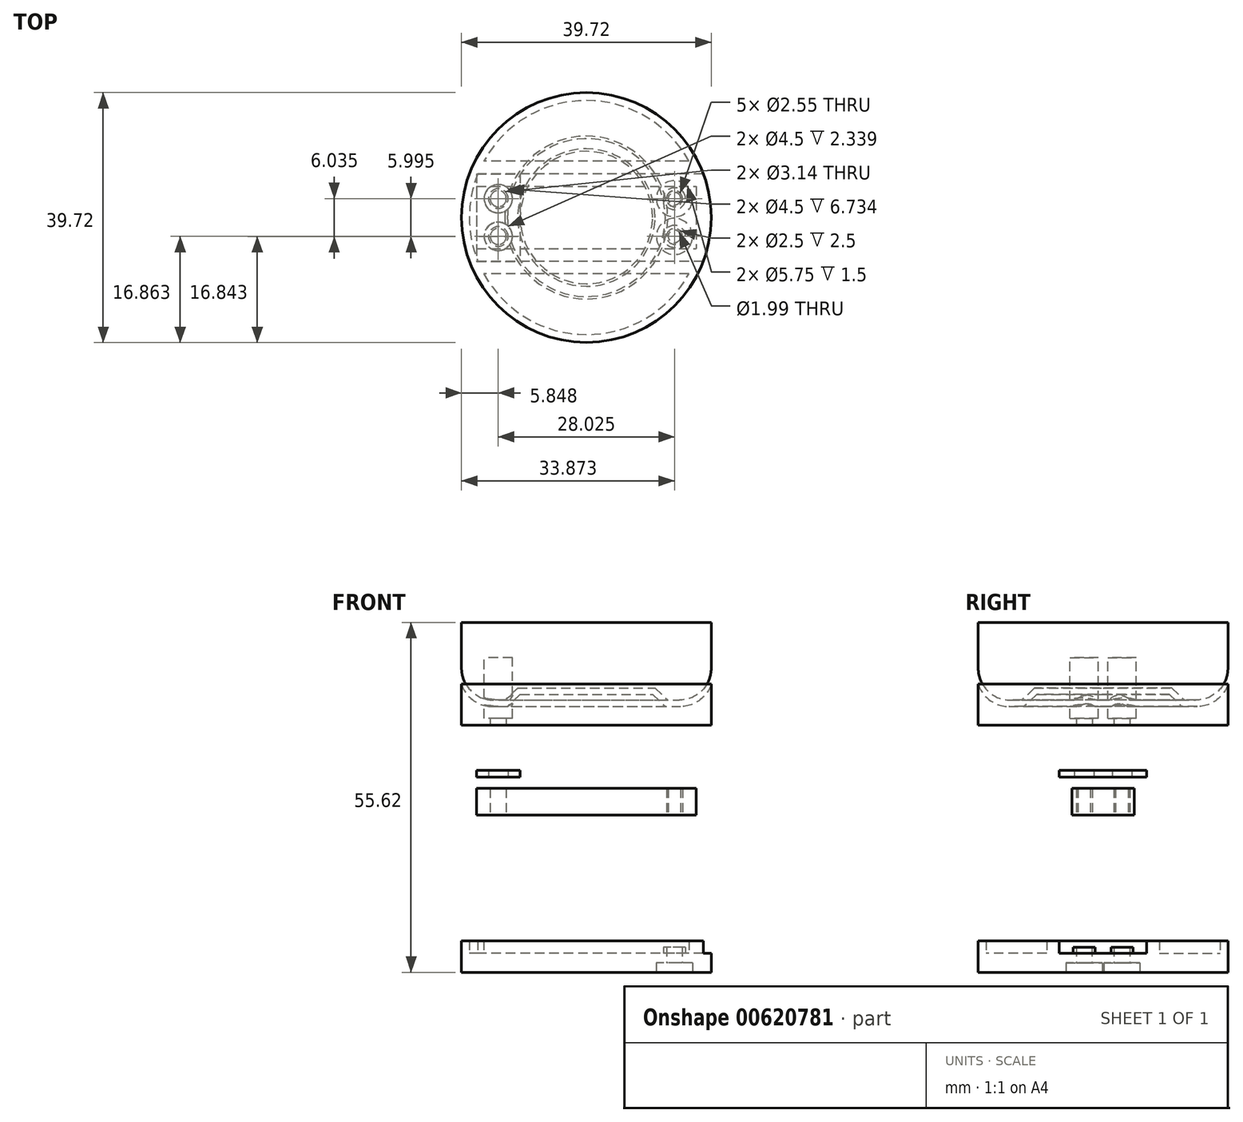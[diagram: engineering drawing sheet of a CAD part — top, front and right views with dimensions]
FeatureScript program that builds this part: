
annotation { "Feature Type Name" : "Feature", "Feature Type Description" : "" }
export const myFeature = defineFeature(function(context is Context, id is Id, definition is map)
    precondition{}
    {
        {
            var Q0;
            Q0=qCreatedBy(makeId("Front.planeOp"),FACE);
            var sketch = newSketch(context, id + "F0", { "sketchPlane" : qUnion([Q0])});
            skLineSegment(sketch, "E0", {"start": v(-12.95, 18.27) * mm, "end": v(-10.93, 20.17) * mm});
            skLineSegment(sketch, "E1", {"start": v(-12.95, 18.27) * mm, "end": v(-14.77, 18.27) * mm});
            skArc(sketch, "E2", {"start": v(-19.86, 23.36) * mm, "mid": v(-18.36, 19.76) * mm, "end": v(-14.77, 18.27) * mm});
            skLineSegment(sketch, "E3", {"start": v(-19.86, 23.36) * mm, "end": v(-19.86, 30.62) * mm});
            skLineSegment(sketch, "E4", {"start": v(0, 0) * mm, "end": v(0, 35.2) * mm, "construction": true});
            skLineSegment(sketch, "E5", {"start": v(-10.92, 20.17) * mm, "end": v(0, 20.17) * mm});
            skLineSegment(sketch, "E6", {"start": v(-19.86, 30.62) * mm, "end": v(0, 30.62) * mm});
            skLineSegment(sketch, "E7.MirrorCS", {"start": v(10.92, 20.17) * mm, "end": v(0, 20.17) * mm, "construction": true});
            skLineSegment(sketch, "E8.MirrorCS", {"start": v(19.86, 30.62) * mm, "end": v(0, 30.62) * mm, "construction": true});
            skLineSegment(sketch, "E9.MirrorCS", {"start": v(12.95, 18.27) * mm, "end": v(10.93, 20.17) * mm, "construction": true});
            skLineSegment(sketch, "E10.MirrorCS", {"start": v(19.86, 23.36) * mm, "end": v(19.86, 30.62) * mm, "construction": true});
            skLineSegment(sketch, "E11.MirrorCS", {"start": v(12.95, 18.27) * mm, "end": v(14.77, 18.27) * mm, "construction": true});
            skArc(sketch, "E12.MirrorCS", {"start": v(19.86, 23.36) * mm, "mid": v(18.36, 19.76) * mm, "end": v(14.77, 18.27) * mm, "construction": true});
            skLineSegment(sketch, "E13", {"start": v(0, 20.17) * mm, "end": v(0, 30.62) * mm});
            skLineSegment(sketch, "E14.0", {"start": v(-12.55, 17.27) * mm, "end": v(-15, 17.27) * mm});
            skLineSegment(sketch, "E14.1", {"start": v(-12.55, 17.27) * mm, "end": v(-10.53, 19.17) * mm});
            skLineSegment(sketch, "E14.2", {"start": v(-10.53, 19.17) * mm, "end": v(0, 19.17) * mm});
            skLineSegment(sketch, "E15", {"start": v(-19.86, 23.36) * mm, "end": v(-19.86, 8.22) * mm, "construction": true});
            skArc(sketch, "E16", {"start": v(-19.86, 20.85) * mm, "mid": v(-18.01, 18.26) * mm, "end": v(-15, 17.27) * mm});
            skLineSegment(sketch, "E17", {"start": v(0, 19.17) * mm, "end": v(0, 14.27) * mm});
            skLineSegment(sketch, "E18", {"start": v(0, 14.27) * mm, "end": v(-19.86, 14.27) * mm});
            skLineSegment(sketch, "E19", {"start": v(-19.86, 14.27) * mm, "end": v(-19.86, 20.85) * mm});
            skSolve(sketch);
        }
        {
            var Q0;
            Q0 = qSketchRegion(id + "F0", true);
            var Q1;
            Q1=sQuery(id+"F0.wireOp",EDGE,"E4");
            revolve(context, id + "F1", {"entities" : qUnion([Q0]), "axis" : qUnion([Q1]), "revolveType" : RevolveType.FULL});
        }
        {
            var Q0;
            Q0=qCreatedBy(makeId("Top.planeOp"),FACE);
            var sketch = newSketch(context, id + "F2", { "sketchPlane" : qUnion([Q0])});
            skLineSegment(sketch, "E20.bottom", {"start": v(-17.46, 4.95) * mm, "end": v(17.46, 4.95) * mm});
            skLineSegment(sketch, "E20.top", {"start": v(-17.46, -4.95) * mm, "end": v(17.46, -4.95) * mm});
            skLineSegment(sketch, "E20.left", {"start": v(-17.46, 4.95) * mm, "end": v(-17.46, -4.95) * mm});
            skLineSegment(sketch, "E20.right", {"start": v(17.46, 4.95) * mm, "end": v(17.46, -4.95) * mm});
            skPoint(sketch, "E20.middle", {"position": v(0, 0) * mm});
            skLineSegment(sketch, "E21", {"start": v(-57.83, 0) * mm, "end": v(44.3, 0) * mm, "construction": true});
            skLineSegment(sketch, "E22", {"start": v(0, -21.78) * mm, "end": v(0, 18.19) * mm, "construction": true});
            skCircle(sketch, "E23", {"center": v(-14.01, 3) * mm, "radius": 1 * mm});
            skCircle(sketch, "E24.MirrorC", {"center": v(-14.01, -3) * mm, "radius": 1 * mm});
            skCircle(sketch, "E25.MirrorC", {"center": v(14.01, 3) * mm, "radius": 1 * mm});
            skCircle(sketch, "E26.MirrorC", {"center": v(14.01, -3) * mm, "radius": 1 * mm});
            skCircle(sketch, "E27", {"center": v(-14.01, 3) * mm, "radius": 1.27 * mm});
            skCircle(sketch, "E28.MirrorC", {"center": v(14.01, 3) * mm, "radius": 1.27 * mm});
            skCircle(sketch, "E29.MirrorC", {"center": v(14.01, -3) * mm, "radius": 1.27 * mm});
            skCircle(sketch, "E30.MirrorC", {"center": v(-14.01, -3) * mm, "radius": 1.27 * mm});
            skCircle(sketch, "E31", {"center": v(0, 0) * mm, "radius": 19.86 * mm, "construction": true});
            skSolve(sketch);
        }
        {
            var Q0;
            Q0 = qSketchRegion(id + "F2", true);
            var Q1;
            Q1=makeQuery(id+"F2.imprint","IMPRINT",FACE,{"disambiguationData":[TD([[makeQuery(id+"F2.imprint","IMPRINT",EDGE,{"derivedFrom":sQuery(id+"F2.wireOp",EDGE,"E23")}),-1.0]])]});
            var Q2;
            Q2=makeQuery(id+"F2.imprint","IMPRINT",FACE,{"disambiguationData":[TD([[makeQuery(id+"F2.imprint","IMPRINT",EDGE,{"derivedFrom":sQuery(id+"F2.wireOp",EDGE,"E24.MirrorC")}),1.0]])]});
            var Q3;
            Q3=makeQuery(id+"F2.imprint","IMPRINT",FACE,{"disambiguationData":[TD([[makeQuery(id+"F2.imprint","IMPRINT",EDGE,{"derivedFrom":sQuery(id+"F2.wireOp",EDGE,"E25.MirrorC")}),1.0]])]});
            var Q4;
            Q4=makeQuery(id+"F2.imprint","IMPRINT",FACE,{"disambiguationData":[TD([[makeQuery(id+"F2.imprint","IMPRINT",EDGE,{"derivedFrom":sQuery(id+"F2.wireOp",EDGE,"E26.MirrorC")}),-1.0]])]});
            extrude(context, id + "F3", {"entities" : qUnion([Q0, Q1, Q2, Q3, Q4]), "depth" : 4.22 * mm, "offsetDistance" : 25 * mm});
        }
        {
            var Q0;
            Q0=makeQuery(id+"F2.imprint","IMPRINT",FACE,{"disambiguationData":[TD([[makeQuery(id+"F2.imprint","IMPRINT",EDGE,{"derivedFrom":sQuery(id+"F2.wireOp",EDGE,"E24.MirrorC")}),1.0]])]});
            var Q1;
            Q1=makeQuery(id+"F2.imprint","IMPRINT",FACE,{"disambiguationData":[TD([[makeQuery(id+"F2.imprint","IMPRINT",EDGE,{"derivedFrom":sQuery(id+"F2.wireOp",EDGE,"E24.MirrorC")}),-1.0]])]});
            var Q2;
            Q2=makeQuery(id+"F2.imprint","IMPRINT",FACE,{"disambiguationData":[TD([[makeQuery(id+"F2.imprint","IMPRINT",EDGE,{"derivedFrom":sQuery(id+"F2.wireOp",EDGE,"E23")}),1.0]])]});
            var Q3;
            Q3=makeQuery(id+"F2.imprint","IMPRINT",FACE,{"disambiguationData":[TD([[makeQuery(id+"F2.imprint","IMPRINT",EDGE,{"derivedFrom":sQuery(id+"F2.wireOp",EDGE,"E23")}),-1.0]])]});
            extrude(context, id + "F4", {"entities" : qUnion([Q0, Q1, Q2, Q3]), "operationType" : NewBodyOperationType.REMOVE, "depth" : 25 * mm, "offsetDistance" : 25 * mm});
        }
        {
            var Q0;
            Q0=qCreatedBy(makeId("Top.planeOp"),FACE);
            cPlane(context, id + "F5", {"entities" : qUnion([Q0]), "cplaneType" : CPlaneType.OFFSET, "offset" : 25 * mm, "width" : 150 * mm, "height" : 150 * mm});
        }
        {
            var Q0;
            Q0=qCreatedBy(id+"F5.planeOp",FACE);
            var sketch = newSketch(context, id + "F6", { "sketchPlane" : qUnion([Q0])});
            skPoint(sketch, "E32", {"position": v(-14.01, 3) * mm});
            skLineSegment(sketch, "E33", {"start": v(-25.43, 0) * mm, "end": v(22.89, 0) * mm, "construction": true});
            skCircle(sketch, "E34", {"center": v(-14.01, 3) * mm, "radius": 2.25 * mm});
            skCircle(sketch, "E35.MirrorC", {"center": v(-14.01, -3) * mm, "radius": 2.25 * mm});
            skSolve(sketch);
        }
        {
            var Q0;
            Q0=qCreatedBy(makeId("Top.planeOp"),FACE);
            cPlane(context, id + "F7", {"entities" : qUnion([Q0]), "cplaneType" : CPlaneType.OFFSET, "offset" : 6 * mm, "width" : 150 * mm, "height" : 150 * mm});
        }
        {
            var Q0;
            Q0=qCreatedBy(id+"F7.planeOp",FACE);
            var sketch = newSketch(context, id + "F8", { "sketchPlane" : qUnion([Q0])});
            skCircle(sketch, "E36", {"center": v(-14.01, 3.02) * mm, "radius": 1.57 * mm});
            skCircle(sketch, "E37", {"center": v(-14.01, -3.02) * mm, "radius": 1.57 * mm});
            skLineSegment(sketch, "E38", {"start": v(-14.01, 3.02) * mm, "end": v(-14.01, -3.02) * mm, "construction": true});
            skPoint(sketch, "E39", {"position": v(-14.01, 0) * mm});
            skLineSegment(sketch, "E40.bottom", {"start": v(-17.46, 6.95) * mm, "end": v(-10.56, 6.95) * mm});
            skLineSegment(sketch, "E40.top", {"start": v(-17.46, -6.95) * mm, "end": v(-10.56, -6.95) * mm});
            skLineSegment(sketch, "E40.left", {"start": v(-17.46, 6.95) * mm, "end": v(-17.46, -6.95) * mm});
            skLineSegment(sketch, "E40.right", {"start": v(-10.56, 6.95) * mm, "end": v(-10.56, -6.95) * mm});
            skSolve(sketch);
        }
        {
            var Q0;
            Q0 = qSketchRegion(id + "F8", true);
            extrude(context, id + "F9", {"entities" : qUnion([Q0]), "depth" : 1.1 * mm, "offsetDistance" : 25 * mm});
        }
        {
            var Q0;
            Q0=qCreatedBy(makeId("Top.planeOp"),FACE);
            cPlane(context, id + "F10", {"entities" : qUnion([Q0]), "cplaneType" : CPlaneType.OFFSET, "offset" : 25 * mm, "oppositeDirection" : true, "width" : 150 * mm, "height" : 150 * mm});
        }
        {
            var Q0;
            Q0=qCreatedBy(id+"F10.planeOp",FACE);
            var sketch = newSketch(context, id + "F11", { "sketchPlane" : qUnion([Q0])});
            skCircle(sketch, "E41", {"center": v(0, 0) * mm, "radius": 19.86 * mm});
            skCircle(sketch, "E42", {"center": v(0, 0) * mm, "radius": 18.6 * mm});
            skLineSegment(sketch, "E43", {"start": v(-17.26, 6.95) * mm, "end": v(17.26, 6.95) * mm});
            skLineSegment(sketch, "E44", {"start": v(-16.31, 8.95) * mm, "end": v(16.31, 8.95) * mm});
            skLineSegment(sketch, "E45", {"start": v(36.89, 0) * mm, "end": v(-27.17, 0) * mm, "construction": true});
            skLineSegment(sketch, "E46", {"start": v(12.09, 4.95) * mm, "end": v(-7.25, 4.94) * mm, "construction": true});
            skLineSegment(sketch, "E47.MirrorCS", {"start": v(-17.26, -6.95) * mm, "end": v(17.26, -6.95) * mm});
            skLineSegment(sketch, "E48.MirrorCS", {"start": v(-16.31, -8.95) * mm, "end": v(16.31, -8.95) * mm});
            skPoint(sketch, "E49", {"position": v(14.01, 3) * mm});
            skPoint(sketch, "E50", {"position": v(14.01, -3) * mm});
            skCircle(sketch, "E51", {"center": v(14.01, 3) * mm, "radius": 1.25 * mm});
            skCircle(sketch, "E52", {"center": v(14.01, -3) * mm, "radius": 1.25 * mm});
            skCircle(sketch, "E53", {"center": v(14.01, 3) * mm, "radius": 1.75 * mm});
            skCircle(sketch, "E54", {"center": v(14.01, -3) * mm, "radius": 1.75 * mm});
            skLineSegment(sketch, "E55", {"start": v(17.26, -6.95) * mm, "end": v(18.6, -6.95) * mm});
            skLineSegment(sketch, "E56", {"start": v(17.26, 6.95) * mm, "end": v(18.6, 6.95) * mm});
            skSolve(sketch);
        }
        {
            var Q0;
            Q0 = qSketchRegion(id + "F11", true);
            var Q1;
            {var subQ0=sQuery(id+"F11.wireOp",EDGE,"E48.MirrorCS");Q1=makeQuery(id+"F11.imprint","IMPRINT",FACE,{"disambiguationData":[TD([[makeQuery(id+"F11.imprint","IMPRINT",EDGE,{"derivedFrom":subQ0}),-1.0]])]});}
            var Q2;
            {var subQ0=sQuery(id+"F11.wireOp",EDGE,"E47.MirrorCS");Q2=makeQuery(id+"F11.imprint","IMPRINT",FACE,{"disambiguationData":[TD([[makeQuery(id+"F11.imprint","IMPRINT",EDGE,{"derivedFrom":subQ0}),-1.0]])]});}
            var Q3;
            {var subQ1=sQuery(id+"F11.wireOp",EDGE,"E43");Q3=makeQuery(id+"F11.imprint","IMPRINT",FACE,{"disambiguationData":[TD([[makeQuery(id+"F11.imprint","IMPRINT",EDGE,{"derivedFrom":subQ1}),-1.0]])]});}
            var Q4;
            {var subQ0=sQuery(id+"F11.wireOp",EDGE,"E43");Q4=makeQuery(id+"F11.imprint","IMPRINT",FACE,{"disambiguationData":[TD([[makeQuery(id+"F11.imprint","IMPRINT",EDGE,{"derivedFrom":subQ0}),1.0]])]});}
            var Q5;
            {var subQ0=sQuery(id+"F11.wireOp",EDGE,"E44");Q5=makeQuery(id+"F11.imprint","IMPRINT",FACE,{"disambiguationData":[TD([[makeQuery(id+"F11.imprint","IMPRINT",EDGE,{"derivedFrom":subQ0}),1.0]])]});}
            var Q6;
            Q6=makeQuery(id+"F11.imprint","IMPRINT",FACE,{"disambiguationData":[TD([[makeQuery(id+"F11.imprint","IMPRINT",EDGE,{"derivedFrom":sQuery(id+"F11.wireOp",EDGE,"E52")}),-1.0]])]});
            var Q7;
            Q7=makeQuery(id+"F11.imprint","IMPRINT",FACE,{"disambiguationData":[TD([[makeQuery(id+"F11.imprint","IMPRINT",EDGE,{"derivedFrom":sQuery(id+"F11.wireOp",EDGE,"E51")}),-1.0]])]});
            extrude(context, id + "F12", {"entities" : qUnion([Q0, Q1, Q2, Q3, Q4, Q5, Q6, Q7]), "depth" : 3 * mm, "offsetDistance" : 25 * mm});
        }
        {
            var Q0;
            Q0=makeQuery(id+"F11.imprint","IMPRINT",FACE,{"disambiguationData":[TD([[makeQuery(id+"F11.imprint","IMPRINT",EDGE,{"derivedFrom":sQuery(id+"F11.wireOp",EDGE,"E52")}),-1.0]])]});
            var Q1;
            Q1=makeQuery(id+"F11.imprint","IMPRINT",FACE,{"disambiguationData":[TD([[makeQuery(id+"F11.imprint","IMPRINT",EDGE,{"derivedFrom":sQuery(id+"F11.wireOp",EDGE,"E51")}),-1.0]])]});
            extrude(context, id + "F13", {"entities" : qUnion([Q0, Q1]), "operationType" : NewBodyOperationType.ADD, "depth" : 4 * mm, "offsetDistance" : 25 * mm});
        }
        {
            var Q0;
            {var subQ0=sQuery(id+"F11.wireOp",EDGE,"E47.MirrorCS");Q0=makeQuery(id+"F11.imprint","IMPRINT",FACE,{"disambiguationData":[TD([[makeQuery(id+"F11.imprint","IMPRINT",EDGE,{"derivedFrom":subQ0}),-1.0]])]});}
            var Q1;
            {var subQ7=sQuery(id+"F11.wireOp",EDGE,"E55");Q1=makeQuery(id+"F11.imprint","IMPRINT",FACE,{"disambiguationData":[TD([[makeQuery(id+"F11.imprint","IMPRINT",EDGE,{"derivedFrom":subQ7}),-1.0]])]});}
            var Q2;
            {var subQ0=sQuery(id+"F11.wireOp",EDGE,"E43");Q2=makeQuery(id+"F11.imprint","IMPRINT",FACE,{"disambiguationData":[TD([[makeQuery(id+"F11.imprint","IMPRINT",EDGE,{"derivedFrom":subQ0}),1.0]])]});}
            extrude(context, id + "F14", {"entities" : qUnion([Q0, Q1, Q2]), "operationType" : NewBodyOperationType.ADD, "depth" : 5 * mm, "offsetDistance" : 25 * mm});
        }
        {
            var Q0;
            Q0 = qSketchRegion(id + "F6", true);
            extrude(context, id + "F15", {"entities" : qUnion([Q0]), "operationType" : NewBodyOperationType.REMOVE, "oppositeDirection" : true, "depth" : 9.63 * mm, "offsetDistance" : 25 * mm});
        }
        {
            var Q0;
            Q0=qCreatedBy(id+"F10.planeOp",FACE);
            var sketch = newSketch(context, id + "F16", { "sketchPlane" : qUnion([Q0])});
            skPoint(sketch, "E57", {"position": v(14.01, -3) * mm});
            skLineSegment(sketch, "E58", {"start": v(-31.5, 0) * mm, "end": v(33.55, 0) * mm, "construction": true});
            skCircle(sketch, "E59", {"center": v(14.01, -3) * mm, "radius": 2.88 * mm});
            skCircle(sketch, "E60.MirrorC", {"center": v(14.01, 3) * mm, "radius": 2.88 * mm});
            skSolve(sketch);
        }
        {
            var Q0;
            Q0 = qSketchRegion(id + "F16", true);
            extrude(context, id + "F17", {"entities" : qUnion([Q0]), "operationType" : NewBodyOperationType.REMOVE, "depth" : 1.5 * mm, "offsetDistance" : 25 * mm});
        }
    });
